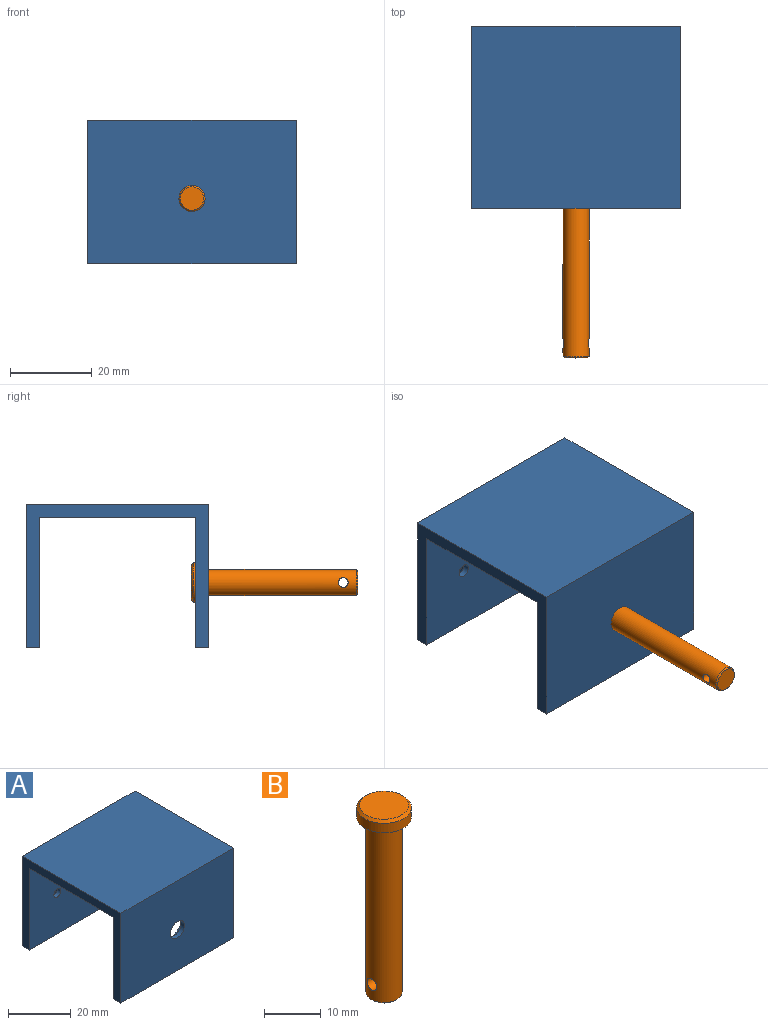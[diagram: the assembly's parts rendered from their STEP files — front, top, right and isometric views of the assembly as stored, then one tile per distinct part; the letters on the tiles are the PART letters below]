
ASSEMBLY  parts=2 mates=1
PART A: 17 faces, bbox 50.8x44.5x34.9 mm
  f0: plane 50.8x44.45mm, normal (0,0,1), area 2258.1mm2, adj f1,f7,f8,f9
  f1: plane 50.8x34.93mm, normal (0,-1,0), area 1742.5mm2, adj f0,f2,f8,f9,f10
  f2: plane 50.8x3.18mm, normal (0,0,-1), area 161.3mm2, adj f1,f3,f8,f9
  f3: plane 50.8x31.75mm, normal (0,1,0), area 1541.6mm2, adj f2,f4,f8,f9,f12
  f4: plane 50.8x38.1mm, normal (0,0,-1), area 1935.5mm2, adj f3,f5,f8,f9
  f5: plane 50.8x31.75mm, normal (0,-1,0), area 1597.1mm2, adj f4,f6,f8,f9,f13,f15
  f6: plane 50.8x3.18mm, normal (0,0,-1), area 161.3mm2, adj f5,f7,f8,f9
  f7: plane 50.8x34.93mm, normal (0,1,0), area 1710.9mm2, adj f0,f6,f8,f9,f14,f16
  f8: plane 44.45x34.93mm, normal (1,0,0), area 342.7mm2, adj f0,f1,f2,f3,f4,f5,f6,f7
  f9: plane 44.45x34.93mm, normal (-1,0,0), area 342.7mm2, adj f0,f1,f2,f3,f4,f5,f6,f7
  f10: cylinder r=3.17mm len=6.35mm, axis (0,1,0), area 31.7mm2, adj f1,f11
  f11: plane 9.53x9.53mm, normal (0,1,0), area 39.6mm2, adj f10,f12
  f12: cylinder r=4.76mm len=9.53mm, axis (0,1,0), area 47.5mm2, adj f3,f11
  f13: cylinder r=1.59mm len=3.18mm, axis (0,1,0), area 15.8mm2, adj f5,f14
  f14: cone r=1.59mm half-angle=45deg, axis (0,1,0), area 33.6mm2, adj f7,f13
  f15: cylinder r=1.59mm len=3.18mm, axis (0,1,0), area 15.8mm2, adj f5,f16
  f16: cone r=1.59mm half-angle=45deg, axis (0,1,0), area 33.6mm2, adj f7,f15
PART B: 8 faces, bbox 9.7x9.7x40.6 mm
  f0: cylinder r=3.17mm len=37.78mm, axis (0,0,-1), area 744.7mm2, adj f2,f6,f7
  f1: plane 5.72x5.72mm, normal (0,0,-1), area 25.7mm2, adj f7
  f2: plane 9.65x9.65mm, normal (0,0,-1), area 41.5mm2, adj f0,f3
  f3: cylinder r=4.83mm len=9.65mm, axis (0,0,-1), area 61.6mm2, adj f2,f5
  f4: plane 8.64x8.64mm, normal (0,0,1), area 58.6mm2, adj f5
  f5: cone r=4.32mm half-angle=45deg, axis (0,0,-1), area 20.6mm2, adj f3,f4
  f6: cylinder r=1.19mm len=6.35mm, axis (1,0,0), area 45.8mm2, adj f0
  f7: cone r=3.17mm half-angle=45deg, axis (0,0,1), area 8.5mm2, adj f0,f1
PLACE A at identity fixed
PLACE B rot(axis=(-1,0,0),90deg) t=(0,-20.64,0)mm
MATE fastened B.f0 <-> A.f10  axis (0,-1,0) through (0,-1.59,0)mm
